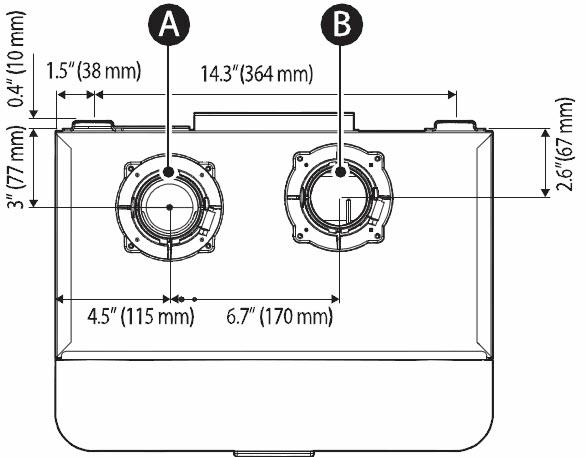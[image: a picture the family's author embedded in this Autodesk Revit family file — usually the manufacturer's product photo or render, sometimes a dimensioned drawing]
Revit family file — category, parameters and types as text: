
# Revit family: Water_Heater-Racks-Navien-NPE-3_Unit_Back_to_Back--
name_source: partatom
category: Mechanical Equipment
revit_build: Autodesk Revit 2016 (Build: 20150220_1215(x64)
units: mm (PartAtom-declared; Revit-internal decimal feet)

## family parameters
Cut with Voids When Loaded = No
Host = Face
OmniClass Number = 23.65.35.11
OmniClass Title = Supply Water Heaters
Part Type = Normal
Room Calculation Point = No
Round Connector Dimension = Use Diameter
Shared = No

## types (4) — shared parameters
2" Exhaust/Intake = Yes
3" Exhaust/Intake = No
Apparent Load = 0 VA
Assembly Code = D3010500
Certifications = Energy Star | AHRI | CSA | CSA | NFS
Cold Water Inlet = 1"
Configuration = NPE_B3_3B
Default Elevation = 48 "
Depth = 23.8 "
Description = 3 Unit Back to Back
Exhaust = 2"
Finish = Metal - Navien - White
Flow Rate = 1 GPM
Flow Rate Note = 35°F (19°C) temp rise: 11.2 GPM (42 L/m) | 45°F (25°C) temp rise: 8.7 GPM (33 L/m) | 67°F (36°C) temp rise: NPE-240A: 5.6 GPM(21 L/m), NPE-240S: 5.7 GPM(22 L/m)
Frequency = 60 Hz
Gas Inlet = 1"
Heating Capacity = 120000.0 Btu/h
Heating Capacity Note = 19,900–199,900 (BTU/H)
Height = 65.5 "
Hot Water Outlet = 1"
Ignition = Electronic ignition
Installation Type = Indoor
Intake = 2"
Keynote = 22 33 00.A1
Manifold(s) = (1) 30019042A
Manufacturer = Navien, Inc.
Manufacturer Fax Number = (949) 420-0430
Natural Gas Manifold Pressure = -0.05" WC to -0.58" WC
Natural Gas Supply Pressure = 3.5"–10.5" WC
Number of Poles = 1
Phase = 1
Power Factor = 1
Product Documentation Link = https://www.navieninc.com
Product Name = NPE Series Tankless Water Heaters w/ Racks
Product Page URL = https://www.navieninc.com
Propane Gas Manifold Pressure = -0.10" WC to -0.78" WC
Propane Gas Supply Pressure = 8"–13" WC
Rack(s) = (1) GFFM-KDIZUS-003 + (1) GFFM-KDIZUS-004
Required Cascade Operation Accessory = (3) 30014367A (Common Vent Damper & Cascade Communication Cable) or (2) GXXX000546 (Individual Vent Cascade Communication Cable)
URL = https://www.navieninc.com
Venting = Exhaust: 2" PVC, CPVC, PP, SS / 2" special gas vent type BH (Class II, A/B/C) | Intake: 2" PVC, CPVC, PP, SS / 2" special gas vent type BH (Class II, A/B/C) | Vent clearances: 0" to combustibles
Venting Type = Forced draft direct vent
Version = 2016 - v1.0.a
Voltage = 120 V
Water Pressure = 15–150 PSI
Wi-Fi Ready = NaviLink Wi-Fi Control: PBCM-AS-001
Width = 42.3 "

## per-type parameters (varying)
| type | Constraints | Model | Natural Gas | Propane Gas | Recirculation Inlet | Recirculation Inlet Visibility | Tankless Water Heaters | Weight |
| Natural Gas - Recirculating System - NPE-240A(Advanced)-NG | 6 | (3) NPE-240A-NG | Yes | No | 0" | Yes | (3) NPE-240A-NG | 82.00 lbf |
| Natural Gas - NPE-240S(Standard)-NG | 7 | (3) NPE-240S-NG | Yes | No | 1" | No | (3) NPE-240S-NG | 75.00 lbf |
| Propane Gas - Recirculating System - NPE-240A(Advanced)-LPG | 6 | (3) NPE-240A-LPG | No | Yes | 0" | Yes | (3) NPE-240A-LPG | 82.00 lbf |
| Propane Gas - NPE-240S(Standard)-LPG | 7 | (3) NPE-240S-LPG | No | Yes | 1" | No | (3) NPE-240S-LPG | 75.00 lbf |

## geometry (parser evidence)
native form markers: Sweep x22
no freeform markers — native parametric forms only
